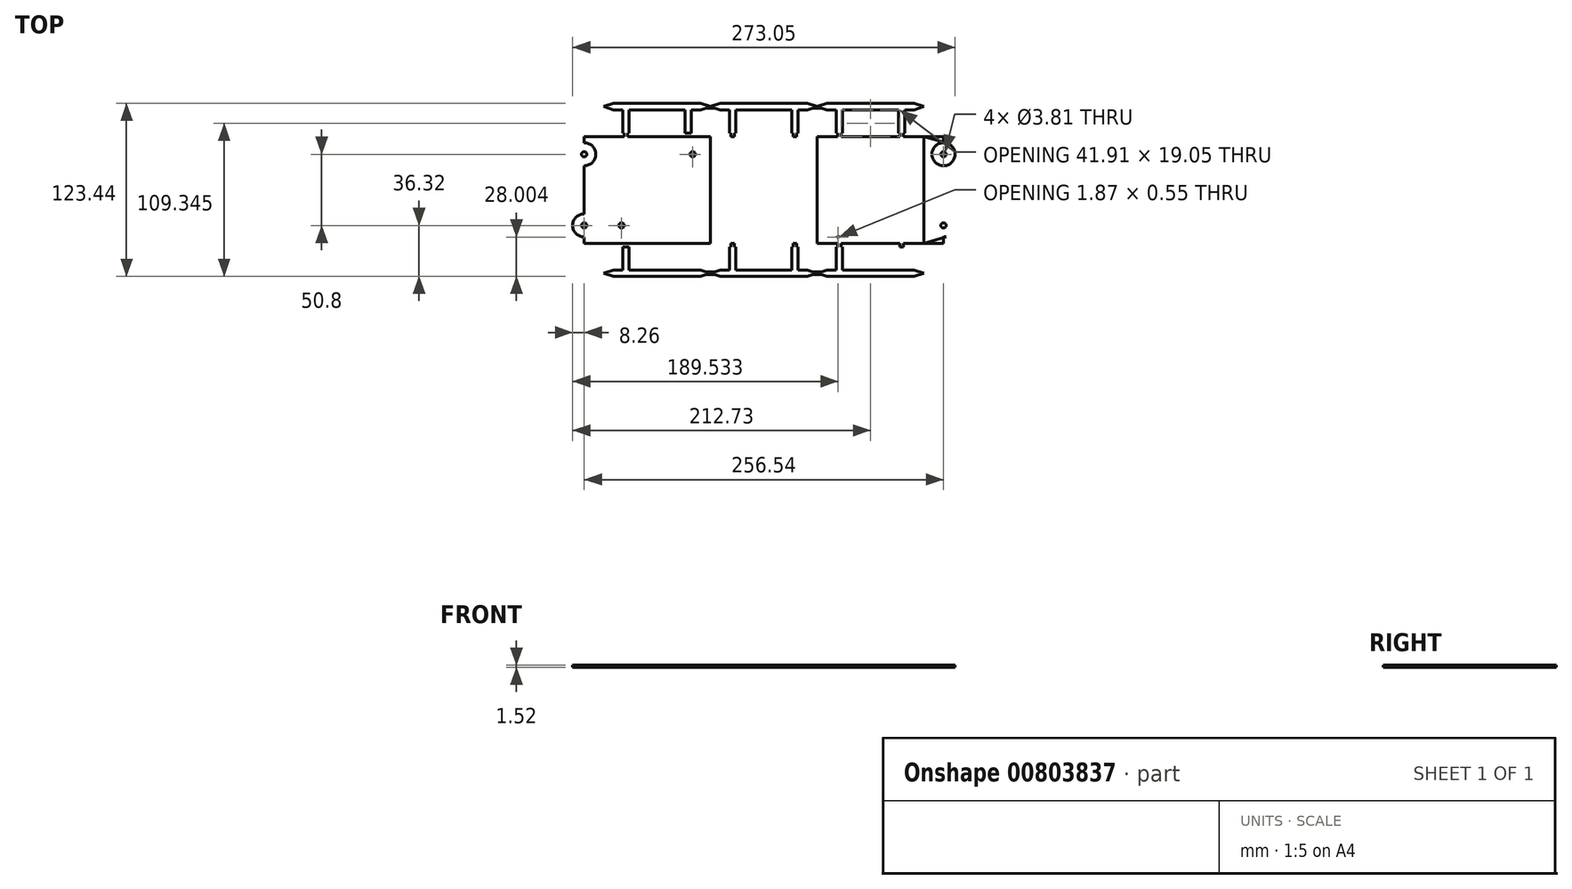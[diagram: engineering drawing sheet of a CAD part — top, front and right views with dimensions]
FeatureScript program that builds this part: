
annotation { "Feature Type Name" : "Feature", "Feature Type Description" : "" }
export const myFeature = defineFeature(function(context is Context, id is Id, definition is map)
    precondition{}
    {
        {
            var Q0;
            Q0=qCreatedBy(makeId("Top.planeOp"),FACE);
            var sketch = newSketch(context, id + "F0", { "sketchPlane" : qUnion([Q0])});
            skLineSegment(sketch, "E0.bottom", {"start": v(38.1, 38.1) * mm, "end": v(-38.1, 38.1) * mm});
            skLineSegment(sketch, "E0.top", {"start": v(38.1, -38.1) * mm, "end": v(-38.1, -38.1) * mm});
            skLineSegment(sketch, "E0.left", {"start": v(38.1, 38.1) * mm, "end": v(38.1, -38.1) * mm});
            skPoint(sketch, "E0.middle", {"position": v(0, 0) * mm});
            skLineSegment(sketch, "E1.bottom", {"start": v(31.75, 31.75) * mm, "end": v(-31.75, 31.75) * mm, "construction": true});
            skLineSegment(sketch, "E1.top", {"start": v(31.75, -31.75) * mm, "end": v(-31.75, -31.75) * mm, "construction": true});
            skLineSegment(sketch, "E1.left", {"start": v(31.75, 31.75) * mm, "end": v(31.75, -31.75) * mm, "construction": true});
            skLineSegment(sketch, "E1.right", {"start": v(-31.75, 31.75) * mm, "end": v(-31.75, -31.75) * mm, "construction": true});
            skLineSegment(sketch, "E2.bottom", {"start": v(-19.18, -31.75) * mm, "end": v(-12.57, -31.75) * mm});
            skLineSegment(sketch, "E2.top", {"start": v(-19.18, -30.23) * mm, "end": v(-12.57, -30.23) * mm});
            skLineSegment(sketch, "E2.left", {"start": v(-19.18, -31.75) * mm, "end": v(-19.18, -30.23) * mm});
            skLineSegment(sketch, "E2.right", {"start": v(-12.57, -31.75) * mm, "end": v(-12.57, -30.23) * mm});
            skPoint(sketch, "E3", {"position": v(-15.88, -31.75) * mm});
            skLineSegment(sketch, "E4.0", {"start": v(-19.43, -29.97) * mm, "end": v(-12.32, -29.97) * mm});
            skLineSegment(sketch, "E4.1", {"start": v(-19.43, -32) * mm, "end": v(-19.43, -29.97) * mm});
            skLineSegment(sketch, "E4.2", {"start": v(-19.43, -32) * mm, "end": v(-12.32, -32) * mm});
            skLineSegment(sketch, "E4.3", {"start": v(-12.32, -32) * mm, "end": v(-12.32, -29.97) * mm});
            skLineSegment(sketch, "E5.MirrorCS", {"start": v(19.43, -29.97) * mm, "end": v(12.32, -29.97) * mm});
            skLineSegment(sketch, "E6.MirrorCS", {"start": v(19.43, -32) * mm, "end": v(19.43, -29.97) * mm});
            skLineSegment(sketch, "E7.MirrorCS", {"start": v(19.43, -32) * mm, "end": v(12.32, -32) * mm});
            skLineSegment(sketch, "E8.MirrorCS", {"start": v(12.32, -32) * mm, "end": v(12.32, -29.97) * mm});
            skLineSegment(sketch, "E9.MirrorCS", {"start": v(-19.43, 32) * mm, "end": v(-19.43, 29.97) * mm});
            skLineSegment(sketch, "E10.MirrorCS", {"start": v(-19.43, 29.97) * mm, "end": v(-12.32, 29.97) * mm});
            skLineSegment(sketch, "E11.MirrorCS", {"start": v(-12.32, 32) * mm, "end": v(-12.32, 29.97) * mm});
            skLineSegment(sketch, "E12.MirrorCS", {"start": v(-19.43, 32) * mm, "end": v(-12.32, 32) * mm});
            skLineSegment(sketch, "E13.MirrorCS", {"start": v(19.43, 29.97) * mm, "end": v(12.32, 29.97) * mm});
            skLineSegment(sketch, "E14.MirrorCS", {"start": v(19.43, 32) * mm, "end": v(19.43, 29.97) * mm});
            skLineSegment(sketch, "E15.MirrorCS", {"start": v(19.43, 32) * mm, "end": v(12.32, 32) * mm});
            skLineSegment(sketch, "E16.MirrorCS", {"start": v(12.32, 32) * mm, "end": v(12.32, 29.97) * mm});
            skLineSegment(sketch, "E17.bottom", {"start": v(-31.75, -19.18) * mm, "end": v(-30.23, -19.18) * mm});
            skLineSegment(sketch, "E17.top", {"start": v(-31.75, -12.57) * mm, "end": v(-30.23, -12.57) * mm});
            skLineSegment(sketch, "E17.left", {"start": v(-31.75, -19.18) * mm, "end": v(-31.75, -12.57) * mm});
            skLineSegment(sketch, "E17.right", {"start": v(-30.23, -19.18) * mm, "end": v(-30.23, -12.57) * mm});
            skPoint(sketch, "E18", {"position": v(-31.75, -15.88) * mm});
            skLineSegment(sketch, "E19.0", {"start": v(-29.97, -19.43) * mm, "end": v(-29.97, -12.32) * mm});
            skLineSegment(sketch, "E19.1", {"start": v(-32, -19.43) * mm, "end": v(-29.97, -19.43) * mm});
            skLineSegment(sketch, "E19.2", {"start": v(-32, -19.43) * mm, "end": v(-32, -12.32) * mm});
            skLineSegment(sketch, "E19.3", {"start": v(-32, -12.32) * mm, "end": v(-29.97, -12.32) * mm});
            skLineSegment(sketch, "E20.MirrorCS", {"start": v(-32, 19.43) * mm, "end": v(-32, 12.32) * mm});
            skLineSegment(sketch, "E21.MirrorCS", {"start": v(-32, 12.32) * mm, "end": v(-29.97, 12.32) * mm});
            skLineSegment(sketch, "E22.MirrorCS", {"start": v(-29.97, 19.43) * mm, "end": v(-29.97, 12.32) * mm});
            skLineSegment(sketch, "E23.MirrorCS", {"start": v(-32, 19.43) * mm, "end": v(-29.97, 19.43) * mm});
            skLineSegment(sketch, "E24.MirrorCS", {"start": v(32, -19.43) * mm, "end": v(32, -12.32) * mm});
            skLineSegment(sketch, "E25.MirrorCS", {"start": v(32, -12.32) * mm, "end": v(29.97, -12.32) * mm});
            skLineSegment(sketch, "E26.MirrorCS", {"start": v(29.97, -19.43) * mm, "end": v(29.97, -12.32) * mm});
            skLineSegment(sketch, "E27.MirrorCS", {"start": v(32, -19.43) * mm, "end": v(29.97, -19.43) * mm});
            skLineSegment(sketch, "E28.MirrorCS", {"start": v(29.97, 19.43) * mm, "end": v(29.97, 12.32) * mm});
            skLineSegment(sketch, "E29.MirrorCS", {"start": v(32, 12.32) * mm, "end": v(29.97, 12.32) * mm});
            skLineSegment(sketch, "E30.MirrorCS", {"start": v(32, 19.43) * mm, "end": v(32, 12.32) * mm});
            skLineSegment(sketch, "E31.MirrorCS", {"start": v(32, 19.43) * mm, "end": v(29.97, 19.43) * mm});
            skLineSegment(sketch, "E32.bottom", {"start": v(-23.5, -38.1) * mm, "end": v(-20.96, -38.1) * mm});
            skLineSegment(sketch, "E32.top", {"start": v(-23.5, -40.64) * mm, "end": v(-20.96, -40.64) * mm});
            skLineSegment(sketch, "E32.left", {"start": v(-23.5, -38.1) * mm, "end": v(-23.5, -40.64) * mm});
            skLineSegment(sketch, "E32.right", {"start": v(-20.96, -38.1) * mm, "end": v(-20.96, -40.64) * mm});
            skPoint(sketch, "E33", {"position": v(-22.23, -38.1) * mm});
            skLineSegment(sketch, "E34.bottom", {"start": v(-24.51, -40.64) * mm, "end": v(-19.94, -40.64) * mm});
            skLineSegment(sketch, "E34.top", {"start": v(-24.51, -57.15) * mm, "end": v(-19.94, -57.15) * mm});
            skLineSegment(sketch, "E34.left", {"start": v(-24.51, -40.64) * mm, "end": v(-24.51, -57.15) * mm});
            skLineSegment(sketch, "E34.right", {"start": v(-19.94, -40.64) * mm, "end": v(-19.94, -57.15) * mm});
            skPoint(sketch, "E35", {"position": v(-22.23, -40.64) * mm});
            skLineSegment(sketch, "E36.MirrorCS", {"start": v(23.5, -38.1) * mm, "end": v(20.96, -38.1) * mm});
            skPoint(sketch, "E37.MirrorP", {"position": v(22.23, -38.1) * mm});
            skLineSegment(sketch, "E38.bottom", {"start": v(0, -57.15) * mm, "end": v(-31.12, -57.15) * mm});
            skLineSegment(sketch, "E38.top", {"start": v(0, -61.72) * mm, "end": v(-31.12, -61.72) * mm});
            skLineSegment(sketch, "E39", {"start": v(-38.1, -59.44) * mm, "end": v(-31.12, -57.15) * mm});
            skLineSegment(sketch, "E40", {"start": v(-38.1, -59.44) * mm, "end": v(-31.12, -61.72) * mm});
            skPoint(sketch, "E41.start.orphan", {"position": v(-31.12, -59.44) * mm});
            skLineSegment(sketch, "E42.MirrorCS", {"start": v(38.1, -38.1) * mm, "end": v(38.1, 38.1) * mm});
            skPoint(sketch, "E43.MirrorP", {"position": v(-38.1, 57.15) * mm});
            skCircle(sketch, "E44", {"center": v(-25.4, 25.4) * mm, "radius": 1.9 * mm});
            skCircle(sketch, "E45.MirrorC", {"center": v(25.4, 25.4) * mm, "radius": 1.9 * mm});
            skCircle(sketch, "E46.MirrorC", {"center": v(-25.4, -25.4) * mm, "radius": 1.9 * mm});
            skCircle(sketch, "E47.MirrorC", {"center": v(25.4, -25.4) * mm, "radius": 1.9 * mm});
            skLineSegment(sketch, "E48", {"start": v(0, 38.1) * mm, "end": v(0, -38.1) * mm, "construction": true});
            skLineSegment(sketch, "E49", {"start": v(0, -38.1) * mm, "end": v(0, -79.98) * mm, "construction": true});
            skLineSegment(sketch, "E50.MirrorCS", {"start": v(24.51, -40.64) * mm, "end": v(19.94, -40.64) * mm});
            skLineSegment(sketch, "E51.MirrorCS", {"start": v(23.5, -40.64) * mm, "end": v(20.96, -40.64) * mm});
            skLineSegment(sketch, "E52.MirrorCS", {"start": v(23.5, -38.1) * mm, "end": v(23.5, -40.64) * mm});
            skLineSegment(sketch, "E53.MirrorCS", {"start": v(20.96, -38.1) * mm, "end": v(20.96, -40.64) * mm});
            skLineSegment(sketch, "E54.MirrorCS", {"start": v(24.51, -57.15) * mm, "end": v(19.94, -57.15) * mm});
            skPoint(sketch, "E55.MirrorP", {"position": v(22.23, -40.64) * mm});
            skLineSegment(sketch, "E56.MirrorCS", {"start": v(0, -57.15) * mm, "end": v(31.12, -57.15) * mm});
            skLineSegment(sketch, "E57.MirrorCS", {"start": v(38.1, -59.44) * mm, "end": v(31.12, -57.15) * mm});
            skLineSegment(sketch, "E58.MirrorCS", {"start": v(38.1, -59.44) * mm, "end": v(31.12, -61.72) * mm});
            skLineSegment(sketch, "E59.MirrorCS", {"start": v(24.51, -40.64) * mm, "end": v(24.51, -57.15) * mm});
            skLineSegment(sketch, "E60.MirrorCS", {"start": v(0, -61.72) * mm, "end": v(31.12, -61.72) * mm});
            skPoint(sketch, "E61.MirrorP", {"position": v(31.12, -59.44) * mm});
            skLineSegment(sketch, "E62.MirrorCS", {"start": v(19.94, -40.64) * mm, "end": v(19.94, -57.15) * mm});
            skLineSegment(sketch, "E63.MirrorCS", {"start": v(-23.5, 40.64) * mm, "end": v(-20.96, 40.64) * mm});
            skLineSegment(sketch, "E64.MirrorCS", {"start": v(-24.51, 40.64) * mm, "end": v(-19.94, 40.64) * mm});
            skPoint(sketch, "E65.MirrorP", {"position": v(22.23, 38.1) * mm});
            skLineSegment(sketch, "E66.MirrorCS", {"start": v(24.51, 40.64) * mm, "end": v(19.94, 40.64) * mm});
            skLineSegment(sketch, "E67.MirrorCS", {"start": v(23.5, 40.64) * mm, "end": v(20.96, 40.64) * mm});
            skPoint(sketch, "E68.MirrorP", {"position": v(-22.23, 38.1) * mm});
            skPoint(sketch, "E69.MirrorP", {"position": v(22.23, 40.64) * mm});
            skPoint(sketch, "E70.MirrorP", {"position": v(-22.23, 40.64) * mm});
            skLineSegment(sketch, "E71.MirrorCS", {"start": v(24.51, 57.15) * mm, "end": v(19.94, 57.15) * mm});
            skLineSegment(sketch, "E72.MirrorCS", {"start": v(-24.51, 57.15) * mm, "end": v(-19.94, 57.15) * mm});
            skLineSegment(sketch, "E73.MirrorCS", {"start": v(24.51, 40.64) * mm, "end": v(24.51, 57.15) * mm});
            skLineSegment(sketch, "E74.MirrorCS", {"start": v(-24.51, 40.64) * mm, "end": v(-24.51, 57.15) * mm});
            skLineSegment(sketch, "E75.MirrorCS", {"start": v(-19.94, 40.64) * mm, "end": v(-19.94, 57.15) * mm});
            skLineSegment(sketch, "E76.MirrorCS", {"start": v(0, 61.72) * mm, "end": v(31.12, 61.72) * mm});
            skLineSegment(sketch, "E77.MirrorCS", {"start": v(-38.1, 59.44) * mm, "end": v(-31.12, 61.72) * mm});
            skLineSegment(sketch, "E78.MirrorCS", {"start": v(19.94, 40.64) * mm, "end": v(19.94, 57.15) * mm});
            skPoint(sketch, "E79.MirrorP", {"position": v(-31.12, 59.44) * mm});
            skLineSegment(sketch, "E80.MirrorCS", {"start": v(-38.1, 59.44) * mm, "end": v(-31.12, 57.15) * mm});
            skLineSegment(sketch, "E81.MirrorCS", {"start": v(0, 57.15) * mm, "end": v(31.12, 57.15) * mm});
            skLineSegment(sketch, "E82.MirrorCS", {"start": v(38.1, 59.44) * mm, "end": v(31.12, 61.72) * mm});
            skLineSegment(sketch, "E83.MirrorCS", {"start": v(0, 61.72) * mm, "end": v(-31.12, 61.72) * mm});
            skPoint(sketch, "E84.MirrorP", {"position": v(31.12, 59.44) * mm});
            skLineSegment(sketch, "E85.MirrorCS", {"start": v(0, 57.15) * mm, "end": v(-31.12, 57.15) * mm});
            skLineSegment(sketch, "E86.MirrorCS", {"start": v(38.1, 59.44) * mm, "end": v(31.12, 57.15) * mm});
            skLineSegment(sketch, "E87.MirrorCS", {"start": v(-23.5, 38.1) * mm, "end": v(-20.96, 38.1) * mm});
            skLineSegment(sketch, "E88.MirrorCS", {"start": v(-20.96, 38.1) * mm, "end": v(-20.96, 40.64) * mm});
            skLineSegment(sketch, "E89.MirrorCS", {"start": v(-23.5, 38.1) * mm, "end": v(-23.5, 40.64) * mm});
            skLineSegment(sketch, "E90.MirrorCS", {"start": v(23.5, 38.1) * mm, "end": v(20.96, 38.1) * mm});
            skLineSegment(sketch, "E91.MirrorCS", {"start": v(20.96, 38.1) * mm, "end": v(20.96, 40.64) * mm});
            skLineSegment(sketch, "E92.MirrorCS", {"start": v(23.5, 38.1) * mm, "end": v(23.5, 40.64) * mm});
            skLineSegment(sketch, "E93", {"start": v(-38.1, -59.44) * mm, "end": v(38.1, -59.44) * mm});
            skLineSegment(sketch, "E94.0", {"start": v(-38.1, -60.45) * mm, "end": v(38.1, -60.45) * mm});
            skLineSegment(sketch, "E95.0", {"start": v(-38.1, -58.42) * mm, "end": v(38.1, -58.42) * mm});
            skLineSegment(sketch, "E96.MirrorCS", {"start": v(-38.1, 58.42) * mm, "end": v(38.1, 58.42) * mm});
            skLineSegment(sketch, "E97.MirrorCS", {"start": v(-38.1, 60.45) * mm, "end": v(38.1, 60.45) * mm});
            skLineSegment(sketch, "E98.MirrorCS", {"start": v(52.7, 38.1) * mm, "end": v(55.25, 38.1) * mm});
            skLineSegment(sketch, "E99.MirrorCS", {"start": v(52.7, 40.64) * mm, "end": v(55.25, 40.64) * mm});
            skLineSegment(sketch, "E100.MirrorCS", {"start": v(52.7, 38.1) * mm, "end": v(52.7, 40.64) * mm});
            skLineSegment(sketch, "E101.MirrorCS", {"start": v(55.25, 38.1) * mm, "end": v(55.25, 40.64) * mm});
            skLineSegment(sketch, "E102.MirrorCS", {"start": v(99.7, 40.64) * mm, "end": v(97.16, 40.64) * mm});
            skLineSegment(sketch, "E103.MirrorCS", {"start": v(99.7, 38.1) * mm, "end": v(97.16, 38.1) * mm});
            skLineSegment(sketch, "E104.MirrorCS", {"start": v(97.16, 38.1) * mm, "end": v(97.16, 40.64) * mm});
            skLineSegment(sketch, "E105.MirrorCS", {"start": v(100.71, 40.64) * mm, "end": v(96.14, 40.64) * mm});
            skLineSegment(sketch, "E106.MirrorCS", {"start": v(99.7, 38.1) * mm, "end": v(99.7, 40.64) * mm});
            skLineSegment(sketch, "E107.MirrorCS", {"start": v(51.69, 40.64) * mm, "end": v(56.26, 40.64) * mm});
            skPoint(sketch, "E108.MirrorP", {"position": v(98.43, 38.1) * mm});
            skPoint(sketch, "E109.MirrorP", {"position": v(53.98, 40.64) * mm});
            skPoint(sketch, "E110.MirrorP", {"position": v(98.43, 40.64) * mm});
            skPoint(sketch, "E111.MirrorP", {"position": v(53.98, 38.1) * mm});
            skLineSegment(sketch, "E112.MirrorCS", {"start": v(38.1, 59.44) * mm, "end": v(45.08, 57.15) * mm});
            skLineSegment(sketch, "E113.MirrorCS", {"start": v(51.69, 57.15) * mm, "end": v(56.26, 57.15) * mm});
            skLineSegment(sketch, "E114.MirrorCS", {"start": v(100.71, 57.15) * mm, "end": v(96.14, 57.15) * mm});
            skLineSegment(sketch, "E115.MirrorCS", {"start": v(38.1, 59.44) * mm, "end": v(45.08, 61.72) * mm});
            skLineSegment(sketch, "E116.MirrorCS", {"start": v(114.3, 59.44) * mm, "end": v(107.32, 61.72) * mm});
            skLineSegment(sketch, "E117.MirrorCS", {"start": v(114.3, 59.44) * mm, "end": v(107.32, 57.15) * mm});
            skLineSegment(sketch, "E118.MirrorCS", {"start": v(38.1, 38.1) * mm, "end": v(114.3, 38.1) * mm});
            skLineSegment(sketch, "E119.MirrorCS", {"start": v(114.3, 60.45) * mm, "end": v(38.1, 60.45) * mm});
            skPoint(sketch, "E120.MirrorP", {"position": v(114.3, 57.15) * mm});
            skLineSegment(sketch, "E121.MirrorCS", {"start": v(76.2, 57.15) * mm, "end": v(45.08, 57.15) * mm});
            skPoint(sketch, "E122.MirrorP", {"position": v(107.32, 59.44) * mm});
            skPoint(sketch, "E123.MirrorP", {"position": v(45.08, 59.44) * mm});
            skLineSegment(sketch, "E124.MirrorCS", {"start": v(51.69, 40.64) * mm, "end": v(51.69, 57.15) * mm});
            skLineSegment(sketch, "E125.MirrorCS", {"start": v(100.71, 40.64) * mm, "end": v(100.71, 57.15) * mm});
            skLineSegment(sketch, "E126.MirrorCS", {"start": v(56.26, 40.64) * mm, "end": v(56.26, 57.15) * mm});
            skLineSegment(sketch, "E127.MirrorCS", {"start": v(96.14, 40.64) * mm, "end": v(96.14, 57.15) * mm});
            skLineSegment(sketch, "E128.MirrorCS", {"start": v(76.2, 61.72) * mm, "end": v(45.08, 61.72) * mm});
            skLineSegment(sketch, "E129.MirrorCS", {"start": v(76.2, 61.72) * mm, "end": v(107.32, 61.72) * mm});
            skLineSegment(sketch, "E130.MirrorCS", {"start": v(114.3, 58.42) * mm, "end": v(38.1, 58.42) * mm});
            skLineSegment(sketch, "E131.MirrorCS", {"start": v(76.2, 57.15) * mm, "end": v(107.32, 57.15) * mm});
            skLineSegment(sketch, "E132.MirrorCS", {"start": v(52.7, -38.1) * mm, "end": v(55.25, -38.1) * mm});
            skLineSegment(sketch, "E133.MirrorCS", {"start": v(52.7, -40.64) * mm, "end": v(55.25, -40.64) * mm});
            skLineSegment(sketch, "E134.MirrorCS", {"start": v(99.7, -38.1) * mm, "end": v(97.16, -38.1) * mm});
            skLineSegment(sketch, "E135.MirrorCS", {"start": v(55.25, -38.1) * mm, "end": v(55.25, -40.64) * mm});
            skLineSegment(sketch, "E136.MirrorCS", {"start": v(97.16, -38.1) * mm, "end": v(97.16, -40.64) * mm});
            skLineSegment(sketch, "E137.MirrorCS", {"start": v(52.7, -38.1) * mm, "end": v(52.7, -40.64) * mm});
            skLineSegment(sketch, "E138.MirrorCS", {"start": v(99.7, -40.64) * mm, "end": v(97.16, -40.64) * mm});
            skLineSegment(sketch, "E139.MirrorCS", {"start": v(99.7, -38.1) * mm, "end": v(99.7, -40.64) * mm});
            skLineSegment(sketch, "E140.MirrorCS", {"start": v(100.71, -40.64) * mm, "end": v(96.14, -40.64) * mm});
            skLineSegment(sketch, "E141.MirrorCS", {"start": v(51.69, -40.64) * mm, "end": v(56.26, -40.64) * mm});
            skLineSegment(sketch, "E142.MirrorCS", {"start": v(38.1, -59.44) * mm, "end": v(45.08, -61.72) * mm});
            skLineSegment(sketch, "E143.MirrorCS", {"start": v(114.3, -59.44) * mm, "end": v(107.32, -61.72) * mm});
            skLineSegment(sketch, "E144.MirrorCS", {"start": v(38.1, -59.44) * mm, "end": v(45.08, -57.15) * mm});
            skLineSegment(sketch, "E145.MirrorCS", {"start": v(51.69, -57.15) * mm, "end": v(56.26, -57.15) * mm});
            skLineSegment(sketch, "E146.MirrorCS", {"start": v(114.3, -59.44) * mm, "end": v(107.32, -57.15) * mm});
            skLineSegment(sketch, "E147.MirrorCS", {"start": v(100.71, -57.15) * mm, "end": v(96.14, -57.15) * mm});
            skPoint(sketch, "E148.MirrorP", {"position": v(98.42, -40.64) * mm});
            skPoint(sketch, "E149.MirrorP", {"position": v(53.97, -38.1) * mm});
            skPoint(sketch, "E150.MirrorP", {"position": v(53.97, -40.64) * mm});
            skLineSegment(sketch, "E151.MirrorCS", {"start": v(114.3, -59.44) * mm, "end": v(38.1, -59.44) * mm});
            skLineSegment(sketch, "E152.MirrorCS", {"start": v(100.71, -40.64) * mm, "end": v(100.71, -57.15) * mm});
            skLineSegment(sketch, "E153.MirrorCS", {"start": v(38.1, -38.1) * mm, "end": v(114.3, -38.1) * mm});
            skLineSegment(sketch, "E154.MirrorCS", {"start": v(96.14, -40.64) * mm, "end": v(96.14, -57.15) * mm});
            skLineSegment(sketch, "E155.MirrorCS", {"start": v(51.69, -40.64) * mm, "end": v(51.69, -57.15) * mm});
            skPoint(sketch, "E156.MirrorP", {"position": v(98.42, -38.1) * mm});
            skPoint(sketch, "E157.MirrorP", {"position": v(107.32, -59.44) * mm});
            skLineSegment(sketch, "E158.MirrorCS", {"start": v(76.2, -38.1) * mm, "end": v(76.2, -79.98) * mm, "construction": true});
            skPoint(sketch, "E159.MirrorP", {"position": v(92.08, -31.75) * mm});
            skLineSegment(sketch, "E160.MirrorCS", {"start": v(76.2, -61.72) * mm, "end": v(45.08, -61.72) * mm});
            skLineSegment(sketch, "E161.MirrorCS", {"start": v(76.2, -61.72) * mm, "end": v(107.32, -61.72) * mm});
            skLineSegment(sketch, "E162.MirrorCS", {"start": v(76.2, -57.15) * mm, "end": v(107.32, -57.15) * mm});
            skPoint(sketch, "E163.MirrorP", {"position": v(45.08, -59.44) * mm});
            skLineSegment(sketch, "E164.MirrorCS", {"start": v(56.26, -40.64) * mm, "end": v(56.26, -57.15) * mm});
            skLineSegment(sketch, "E165.MirrorCS", {"start": v(76.2, -57.15) * mm, "end": v(45.08, -57.15) * mm});
            skLineSegment(sketch, "E166.MirrorCS", {"start": v(114.3, -60.45) * mm, "end": v(38.1, -60.45) * mm});
            skLineSegment(sketch, "E167.MirrorCS", {"start": v(114.3, -58.42) * mm, "end": v(38.1, -58.42) * mm});
            skLineSegment(sketch, "E168", {"start": v(-38.1, 38.1) * mm, "end": v(-38.1, -38.1) * mm});
            skCircle(sketch, "E169", {"center": v(-52.07, -25.4) * mm, "radius": 1.9 * mm});
            skCircle(sketch, "E170.0", {"center": v(-52.07, -25.4) * mm, "radius": 8.25 * mm});
            skLineSegment(sketch, "E171", {"start": v(-38.1, -38.1) * mm, "end": v(-53.94, -33.44) * mm});
            skCircle(sketch, "E172.MirrorC", {"center": v(-52.07, 25.4) * mm, "radius": 1.9 * mm});
            skCircle(sketch, "E173.MirrorC", {"center": v(-52.07, 25.4) * mm, "radius": 8.25 * mm});
            skLineSegment(sketch, "E174.MirrorCS", {"start": v(-38.1, 38.1) * mm, "end": v(-53.94, 33.44) * mm});
            skLineSegment(sketch, "E175", {"start": v(-52.07, -17.14) * mm, "end": v(-52.07, 17.14) * mm});
            skCircle(sketch, "E176.MirrorC", {"center": v(128.27, -25.4) * mm, "radius": 1.9 * mm});
            skCircle(sketch, "E177.MirrorC", {"center": v(128.27, -25.4) * mm, "radius": 8.25 * mm});
            skCircle(sketch, "E178.MirrorC", {"center": v(128.27, 25.4) * mm, "radius": 1.9 * mm});
            skLineSegment(sketch, "E179.MirrorCS", {"start": v(114.3, 38.1) * mm, "end": v(130.14, 33.44) * mm});
            skCircle(sketch, "E180.MirrorC", {"center": v(128.27, 25.4) * mm, "radius": 8.25 * mm});
            skLineSegment(sketch, "E181.MirrorCS", {"start": v(114.3, 38.1) * mm, "end": v(114.3, -38.1) * mm});
            skLineSegment(sketch, "E182.MirrorCS", {"start": v(114.3, -38.1) * mm, "end": v(130.14, -33.44) * mm});
            skLineSegment(sketch, "E183.MirrorCS", {"start": v(128.27, -17.15) * mm, "end": v(128.27, 17.14) * mm});
            skLineSegment(sketch, "E184", {"start": v(-52.07, -33.65) * mm, "end": v(-52.07, -38.1) * mm});
            skLineSegment(sketch, "E185", {"start": v(-52.07, -38.1) * mm, "end": v(-38.1, -38.1) * mm});
            skLineSegment(sketch, "E186.MirrorCS", {"start": v(-52.07, 38.1) * mm, "end": v(-38.1, 38.1) * mm});
            skLineSegment(sketch, "E187.MirrorCS", {"start": v(-52.07, 33.65) * mm, "end": v(-52.07, 38.1) * mm});
            skLineSegment(sketch, "E188.MirrorCS", {"start": v(128.27, 33.65) * mm, "end": v(128.27, 38.1) * mm});
            skLineSegment(sketch, "E189.MirrorCS", {"start": v(128.27, 38.1) * mm, "end": v(114.3, 38.1) * mm});
            skLineSegment(sketch, "E190.MirrorCS", {"start": v(128.27, -38.1) * mm, "end": v(114.3, -38.1) * mm});
            skLineSegment(sketch, "E191.MirrorCS", {"start": v(128.27, -33.66) * mm, "end": v(128.27, -38.1) * mm});
            skLineSegment(sketch, "E192.MirrorCS", {"start": v(175.9, 40.64) * mm, "end": v(173.36, 40.64) * mm});
            skLineSegment(sketch, "E193.MirrorCS", {"start": v(175.9, 38.1) * mm, "end": v(173.36, 38.1) * mm});
            skLineSegment(sketch, "E194.MirrorCS", {"start": v(176.91, 40.64) * mm, "end": v(172.34, 40.64) * mm});
            skLineSegment(sketch, "E195.MirrorCS", {"start": v(128.9, 38.1) * mm, "end": v(131.45, 38.1) * mm});
            skLineSegment(sketch, "E196.MirrorCS", {"start": v(127.89, 40.64) * mm, "end": v(132.46, 40.64) * mm});
            skLineSegment(sketch, "E197.MirrorCS", {"start": v(128.9, 40.64) * mm, "end": v(131.45, 40.64) * mm});
            skLineSegment(sketch, "E198.MirrorCS", {"start": v(175.9, 38.1) * mm, "end": v(175.9, 40.64) * mm});
            skLineSegment(sketch, "E199.MirrorCS", {"start": v(131.45, 38.1) * mm, "end": v(131.45, 40.64) * mm});
            skLineSegment(sketch, "E200.MirrorCS", {"start": v(128.9, 38.1) * mm, "end": v(128.9, 40.64) * mm});
            skLineSegment(sketch, "E201.MirrorCS", {"start": v(173.36, 38.1) * mm, "end": v(173.36, 40.64) * mm});
            skLineSegment(sketch, "E202.MirrorCS", {"start": v(128.9, -40.64) * mm, "end": v(131.44, -40.64) * mm});
            skLineSegment(sketch, "E203.MirrorCS", {"start": v(175.9, -38.1) * mm, "end": v(173.36, -38.1) * mm});
            skLineSegment(sketch, "E204.MirrorCS", {"start": v(127.89, -40.64) * mm, "end": v(132.46, -40.64) * mm});
            skLineSegment(sketch, "E205.MirrorCS", {"start": v(128.9, -38.1) * mm, "end": v(131.44, -38.1) * mm});
            skLineSegment(sketch, "E206.MirrorCS", {"start": v(175.9, -38.1) * mm, "end": v(175.9, -40.64) * mm});
            skLineSegment(sketch, "E207.MirrorCS", {"start": v(131.44, -38.1) * mm, "end": v(131.44, -40.64) * mm});
            skLineSegment(sketch, "E208.MirrorCS", {"start": v(176.91, -40.64) * mm, "end": v(172.34, -40.64) * mm});
            skLineSegment(sketch, "E209.MirrorCS", {"start": v(128.9, -38.1) * mm, "end": v(128.9, -40.64) * mm});
            skLineSegment(sketch, "E210.MirrorCS", {"start": v(175.9, -40.64) * mm, "end": v(173.36, -40.64) * mm});
            skLineSegment(sketch, "E211.MirrorCS", {"start": v(173.36, -38.1) * mm, "end": v(173.36, -40.64) * mm});
            skPoint(sketch, "E212.MirrorP", {"position": v(130.18, 40.64) * mm});
            skPoint(sketch, "E213.MirrorP", {"position": v(174.63, 38.1) * mm});
            skPoint(sketch, "E214.MirrorP", {"position": v(174.63, 40.64) * mm});
            skLineSegment(sketch, "E215.MirrorCS", {"start": v(114.3, 59.44) * mm, "end": v(121.28, 57.15) * mm});
            skLineSegment(sketch, "E216.MirrorCS", {"start": v(114.3, -59.44) * mm, "end": v(121.28, -57.15) * mm});
            skLineSegment(sketch, "E217.MirrorCS", {"start": v(114.3, -59.44) * mm, "end": v(121.28, -61.72) * mm});
            skLineSegment(sketch, "E218.MirrorCS", {"start": v(127.89, -57.15) * mm, "end": v(132.46, -57.15) * mm});
            skLineSegment(sketch, "E219.MirrorCS", {"start": v(114.3, 59.44) * mm, "end": v(121.28, 61.72) * mm});
            skLineSegment(sketch, "E220.MirrorCS", {"start": v(176.91, 57.15) * mm, "end": v(172.34, 57.15) * mm});
            skLineSegment(sketch, "E221.MirrorCS", {"start": v(190.5, 59.44) * mm, "end": v(183.52, 57.15) * mm});
            skLineSegment(sketch, "E222.MirrorCS", {"start": v(190.5, -59.44) * mm, "end": v(183.52, -61.72) * mm});
            skLineSegment(sketch, "E223.MirrorCS", {"start": v(190.5, -59.44) * mm, "end": v(183.52, -57.15) * mm});
            skLineSegment(sketch, "E224.MirrorCS", {"start": v(176.91, -57.15) * mm, "end": v(172.34, -57.15) * mm});
            skLineSegment(sketch, "E225.MirrorCS", {"start": v(127.89, 57.15) * mm, "end": v(132.46, 57.15) * mm});
            skLineSegment(sketch, "E226.MirrorCS", {"start": v(190.5, 59.44) * mm, "end": v(183.52, 61.72) * mm});
            skLineSegment(sketch, "E227.MirrorCS", {"start": v(114.3, -60.45) * mm, "end": v(190.5, -60.45) * mm});
            skLineSegment(sketch, "E228.MirrorCS", {"start": v(114.3, 58.42) * mm, "end": v(190.5, 58.42) * mm});
            skPoint(sketch, "E229.MirrorP", {"position": v(174.63, -38.1) * mm});
            skPoint(sketch, "E230.MirrorP", {"position": v(130.18, 38.1) * mm});
            skLineSegment(sketch, "E231.MirrorCS", {"start": v(190.5, 38.1) * mm, "end": v(114.3, 38.1) * mm});
            skLineSegment(sketch, "E232.MirrorCS", {"start": v(190.5, -38.1) * mm, "end": v(190.5, 38.1) * mm});
            skPoint(sketch, "E233.MirrorP", {"position": v(130.18, -40.64) * mm});
            skPoint(sketch, "E234.MirrorP", {"position": v(174.63, -40.64) * mm});
            skPoint(sketch, "E235.MirrorP", {"position": v(130.18, -38.1) * mm});
            skLineSegment(sketch, "E236.MirrorCS", {"start": v(152.4, 61.72) * mm, "end": v(121.28, 61.72) * mm});
            skLineSegment(sketch, "E237.MirrorCS", {"start": v(127.89, 40.64) * mm, "end": v(127.89, 57.15) * mm});
            skLineSegment(sketch, "E238.MirrorCS", {"start": v(190.5, 38.1) * mm, "end": v(190.5, -38.1) * mm});
            skLineSegment(sketch, "E239.MirrorCS", {"start": v(152.4, -57.15) * mm, "end": v(121.28, -57.15) * mm});
            skLineSegment(sketch, "E240.MirrorCS", {"start": v(152.4, -61.72) * mm, "end": v(183.52, -61.72) * mm});
            skLineSegment(sketch, "E241.MirrorCS", {"start": v(152.4, 57.15) * mm, "end": v(121.28, 57.15) * mm});
            skPoint(sketch, "E242.MirrorP", {"position": v(183.52, 59.44) * mm});
            skLineSegment(sketch, "E243.MirrorCS", {"start": v(127.89, -40.64) * mm, "end": v(127.89, -57.15) * mm});
            skLineSegment(sketch, "E244.MirrorCS", {"start": v(152.4, -57.15) * mm, "end": v(183.52, -57.15) * mm});
            skPoint(sketch, "E245.MirrorP", {"position": v(121.28, -59.44) * mm});
            skLineSegment(sketch, "E246.MirrorCS", {"start": v(152.4, 57.15) * mm, "end": v(183.52, 57.15) * mm});
            skLineSegment(sketch, "E247.MirrorCS", {"start": v(132.46, 40.64) * mm, "end": v(132.46, 57.15) * mm});
            skLineSegment(sketch, "E248.MirrorCS", {"start": v(152.4, -38.1) * mm, "end": v(152.4, -79.98) * mm, "construction": true});
            skPoint(sketch, "E249.MirrorP", {"position": v(121.28, 59.44) * mm});
            skLineSegment(sketch, "E250.MirrorCS", {"start": v(190.5, -38.1) * mm, "end": v(114.3, -38.1) * mm});
            skLineSegment(sketch, "E251.MirrorCS", {"start": v(114.3, -58.42) * mm, "end": v(190.5, -58.42) * mm});
            skLineSegment(sketch, "E252.MirrorCS", {"start": v(176.91, 40.64) * mm, "end": v(176.91, 57.15) * mm});
            skPoint(sketch, "E253.MirrorP", {"position": v(197.48, -59.44) * mm});
            skLineSegment(sketch, "E254.MirrorCS", {"start": v(176.91, -40.64) * mm, "end": v(176.91, -57.15) * mm});
            skPoint(sketch, "E255.MirrorP", {"position": v(183.52, -59.44) * mm});
            skLineSegment(sketch, "E256.MirrorCS", {"start": v(132.46, -40.64) * mm, "end": v(132.46, -57.15) * mm});
            skLineSegment(sketch, "E257.MirrorCS", {"start": v(172.34, -40.64) * mm, "end": v(172.34, -57.15) * mm});
            skLineSegment(sketch, "E258.MirrorCS", {"start": v(114.3, -59.44) * mm, "end": v(190.5, -59.44) * mm});
            skLineSegment(sketch, "E259.MirrorCS", {"start": v(152.4, -61.72) * mm, "end": v(121.28, -61.72) * mm});
            skPoint(sketch, "E260.MirrorP", {"position": v(136.53, -31.75) * mm});
            skLineSegment(sketch, "E261.MirrorCS", {"start": v(114.3, 60.45) * mm, "end": v(190.5, 60.45) * mm});
            skLineSegment(sketch, "E262.MirrorCS", {"start": v(172.34, 40.64) * mm, "end": v(172.34, 57.15) * mm});
            skPoint(sketch, "E263.MirrorP", {"position": v(197.48, 59.44) * mm});
            skLineSegment(sketch, "E264.MirrorCS", {"start": v(152.4, 61.72) * mm, "end": v(183.52, 61.72) * mm});
            skLineSegment(sketch, "E265", {"start": v(76.2, 38.1) * mm, "end": v(76.2, -38.1) * mm, "construction": true});
            skCircle(sketch, "E266.MirrorC", {"center": v(204.47, -25.4) * mm, "radius": 1.9 * mm});
            skLineSegment(sketch, "E267.MirrorCS", {"start": v(204.47, -33.66) * mm, "end": v(204.47, -38.1) * mm});
            skCircle(sketch, "E268.MirrorC", {"center": v(204.47, 25.4) * mm, "radius": 1.9 * mm});
            skLineSegment(sketch, "E269.MirrorCS", {"start": v(204.47, -38.1) * mm, "end": v(190.5, -38.1) * mm});
            skLineSegment(sketch, "E270.MirrorCS", {"start": v(190.5, -38.1) * mm, "end": v(206.34, -33.44) * mm});
            skLineSegment(sketch, "E271.MirrorCS", {"start": v(204.47, 33.65) * mm, "end": v(204.47, 38.1) * mm});
            skLineSegment(sketch, "E272.MirrorCS", {"start": v(190.5, 38.1) * mm, "end": v(206.34, 33.44) * mm});
            skLineSegment(sketch, "E273.MirrorCS", {"start": v(204.47, -17.15) * mm, "end": v(204.47, 17.14) * mm});
            skLineSegment(sketch, "E274.MirrorCS", {"start": v(204.47, 38.1) * mm, "end": v(190.5, 38.1) * mm});
            skCircle(sketch, "E275.MirrorC", {"center": v(204.47, -25.4) * mm, "radius": 8.25 * mm});
            skCircle(sketch, "E276.MirrorC", {"center": v(204.47, 25.4) * mm, "radius": 8.25 * mm});
            skSolve(sketch);
        }
        {
            var Q0;
            {var subQ1=sQuery(id+"F0.wireOp",EDGE,"E74.MirrorCS");Q0=makeQuery(id+"F0.imprint","IMPRINT",FACE,{"disambiguationData":[TD([[makeQuery(id+"F0.imprint","IMPRINT",EDGE,{"derivedFrom":subQ1}),-1.0]])]});}
            var Q1;
            {var subQ0=sQuery(id+"F0.wireOp",EDGE,"E121.MirrorCS");var subQ3=sQuery(id+"F0.wireOp",EDGE,"E112.MirrorCS");var subQ4=makeQuery(id+"F0.imprint","INTERSECT",VERTEX,{"derivedFrom":[subQ3,subQ0]});Q1=makeQuery(id+"F0.imprint","IMPRINT",FACE,{"disambiguationData":[TD([[makeQuery(id+"F0.imprint","IMPRINT",EDGE,{"disambiguationData":[TD([[subQ4,1.0]])],"derivedFrom":subQ3}),1.0]])]});}
            var Q2;
            {var subQ5=sQuery(id+"F0.wireOp",EDGE,"E85.MirrorCS");var subQ7=sQuery(id+"F0.wireOp",EDGE,"E80.MirrorCS");var subQ8=makeQuery(id+"F0.imprint","INTERSECT",VERTEX,{"derivedFrom":[subQ7,subQ5]});Q2=makeQuery(id+"F0.imprint","IMPRINT",FACE,{"disambiguationData":[TD([[makeQuery(id+"F0.imprint","IMPRINT",EDGE,{"disambiguationData":[TD([[subQ8,1.0]])],"derivedFrom":subQ7}),1.0]])]});}
            var Q3;
            {var subQ6=sQuery(id+"F0.wireOp",EDGE,"E128.MirrorCS");Q3=makeQuery(id+"F0.imprint","IMPRINT",FACE,{"disambiguationData":[TD([[makeQuery(id+"F0.imprint","IMPRINT",EDGE,{"derivedFrom":subQ6}),1.0]])]});}
            var Q4;
            {var subQ1=sQuery(id+"F0.wireOp",EDGE,"E76.MirrorCS");Q4=makeQuery(id+"F0.imprint","IMPRINT",FACE,{"disambiguationData":[TD([[makeQuery(id+"F0.imprint","IMPRINT",EDGE,{"derivedFrom":subQ1}),-1.0]])]});}
            var Q5;
            {var subQ5=sQuery(id+"F0.wireOp",EDGE,"E80.MirrorCS");var subQ6=sQuery(id+"F0.wireOp",EDGE,"E77.MirrorCS");var subQ7=makeQuery(id+"F0.imprint","INTERSECT",VERTEX,{"derivedFrom":[subQ6,subQ5]});Q5=makeQuery(id+"F0.imprint","IMPRINT",FACE,{"disambiguationData":[TD([[makeQuery(id+"F0.imprint","IMPRINT",EDGE,{"disambiguationData":[TD([[subQ7,-1.0]])],"derivedFrom":subQ6}),-1.0]])]});}
            var Q6;
            {var subQ3=sQuery(id+"F0.wireOp",EDGE,"E97.MirrorCS");var subQ5=sQuery(id+"F0.wireOp",EDGE,"E119.MirrorCS");var subQ6=makeQuery(id+"F0.imprint","INTERSECT",VERTEX,{"derivedFrom":[subQ3,subQ5]});Q6=makeQuery(id+"F0.imprint","IMPRINT",FACE,{"disambiguationData":[TD([[makeQuery(id+"F0.imprint","IMPRINT",EDGE,{"disambiguationData":[TD([[subQ6,1.0]])],"derivedFrom":subQ3}),-1.0]])]});}
            var Q7;
            {var subQ5=sQuery(id+"F0.wireOp",EDGE,"E119.MirrorCS");var subQ9=sQuery(id+"F0.wireOp",EDGE,"E115.MirrorCS");var subQ11=makeQuery(id+"F0.imprint","INTERSECT",VERTEX,{"derivedFrom":[subQ9,subQ5]});Q7=makeQuery(id+"F0.imprint","IMPRINT",FACE,{"disambiguationData":[TD([[makeQuery(id+"F0.imprint","IMPRINT",EDGE,{"disambiguationData":[TD([[subQ11,1.0]])],"derivedFrom":subQ5}),1.0]])]});}
            var Q8;
            {var subQ3=sQuery(id+"F0.wireOp",EDGE,"E96.MirrorCS");var subQ5=sQuery(id+"F0.wireOp",EDGE,"E130.MirrorCS");var subQ6=makeQuery(id+"F0.imprint","INTERSECT",VERTEX,{"derivedFrom":[subQ3,subQ5]});Q8=makeQuery(id+"F0.imprint","IMPRINT",FACE,{"disambiguationData":[TD([[makeQuery(id+"F0.imprint","IMPRINT",EDGE,{"disambiguationData":[TD([[subQ6,1.0]])],"derivedFrom":subQ3}),1.0]])]});}
            var Q9;
            {var subQ1=sQuery(id+"F0.wireOp",EDGE,"E73.MirrorCS");Q9=makeQuery(id+"F0.imprint","IMPRINT",FACE,{"disambiguationData":[TD([[makeQuery(id+"F0.imprint","IMPRINT",EDGE,{"derivedFrom":subQ1}),1.0]])]});}
            var Q10;
            {var subQ4=sQuery(id+"F0.wireOp",EDGE,"E124.MirrorCS");Q10=makeQuery(id+"F0.imprint","IMPRINT",FACE,{"disambiguationData":[TD([[makeQuery(id+"F0.imprint","IMPRINT",EDGE,{"derivedFrom":subQ4}),-1.0]])]});}
            var Q11;
            {var subQ4=sQuery(id+"F0.wireOp",EDGE,"E125.MirrorCS");Q11=makeQuery(id+"F0.imprint","IMPRINT",FACE,{"disambiguationData":[TD([[makeQuery(id+"F0.imprint","IMPRINT",EDGE,{"derivedFrom":subQ4}),1.0]])]});}
            var Q12;
            Q12=makeQuery(id+"F0.imprint","IMPRINT",FACE,{"disambiguationData":[TD([[makeQuery(id+"F0.imprint","IMPRINT",EDGE,{"derivedFrom":sQuery(id+"F0.wireOp",EDGE,"E63.MirrorCS")}),-1.0]])]});
            var Q13;
            {var subQ0=sQuery(id+"F0.wireOp",EDGE,"E104.MirrorCS");Q13=makeQuery(id+"F0.imprint","IMPRINT",FACE,{"disambiguationData":[TD([[makeQuery(id+"F0.imprint","IMPRINT",EDGE,{"derivedFrom":subQ0}),-1.0]])]});}
            var Q14;
            Q14=makeQuery(id+"F0.imprint","IMPRINT",FACE,{"disambiguationData":[TD([[makeQuery(id+"F0.imprint","IMPRINT",EDGE,{"derivedFrom":sQuery(id+"F0.wireOp",EDGE,"E90.MirrorCS")}),-1.0]])]});
            var Q15;
            {var subQ0=sQuery(id+"F0.wireOp",EDGE,"E100.MirrorCS");Q15=makeQuery(id+"F0.imprint","IMPRINT",FACE,{"disambiguationData":[TD([[makeQuery(id+"F0.imprint","IMPRINT",EDGE,{"derivedFrom":subQ0}),-1.0]])]});}
            var Q16;
            {var subQ5=sQuery(id+"F0.wireOp",EDGE,"E42.MirrorCS");Q16=makeQuery(id+"F0.imprint","IMPRINT",FACE,{"disambiguationData":[TD([[makeQuery(id+"F0.imprint","IMPRINT",EDGE,{"derivedFrom":subQ5}),-1.0]])]});}
            var Q17;
            {var subQ4=sQuery(id+"F0.wireOp",EDGE,"E152.MirrorCS");Q17=makeQuery(id+"F0.imprint","IMPRINT",FACE,{"disambiguationData":[TD([[makeQuery(id+"F0.imprint","IMPRINT",EDGE,{"derivedFrom":subQ4}),-1.0]])]});}
            var Q18;
            {var subQ0=sQuery(id+"F0.wireOp",EDGE,"E155.MirrorCS");Q18=makeQuery(id+"F0.imprint","IMPRINT",FACE,{"disambiguationData":[TD([[makeQuery(id+"F0.imprint","IMPRINT",EDGE,{"derivedFrom":subQ0}),1.0]])]});}
            var Q19;
            {var subQ0=sQuery(id+"F0.wireOp",EDGE,"E151.MirrorCS");Q19=makeQuery(id+"F0.imprint","IMPRINT",FACE,{"disambiguationData":[TD([[makeQuery(id+"F0.imprint","IMPRINT",EDGE,{"derivedFrom":subQ0}),-1.0]])]});}
            var Q20;
            {var subQ0=sQuery(id+"F0.wireOp",EDGE,"E160.MirrorCS");Q20=makeQuery(id+"F0.imprint","IMPRINT",FACE,{"disambiguationData":[TD([[makeQuery(id+"F0.imprint","IMPRINT",EDGE,{"derivedFrom":subQ0}),-1.0]])]});}
            var Q21;
            {var subQ2=sQuery(id+"F0.wireOp",EDGE,"E165.MirrorCS");var subQ5=sQuery(id+"F0.wireOp",EDGE,"E144.MirrorCS");var subQ11=makeQuery(id+"F0.imprint","INTERSECT",VERTEX,{"derivedFrom":[subQ5,subQ2]});Q21=makeQuery(id+"F0.imprint","IMPRINT",FACE,{"disambiguationData":[TD([[makeQuery(id+"F0.imprint","IMPRINT",EDGE,{"disambiguationData":[TD([[subQ11,1.0]])],"derivedFrom":subQ5}),-1.0]])]});}
            var Q22;
            {var subQ0=sQuery(id+"F0.wireOp",EDGE,"E151.MirrorCS");Q22=makeQuery(id+"F0.imprint","IMPRINT",FACE,{"disambiguationData":[TD([[makeQuery(id+"F0.imprint","IMPRINT",EDGE,{"derivedFrom":subQ0}),1.0]])]});}
            var Q23;
            {var subQ0=sQuery(id+"F0.wireOp",EDGE,"E136.MirrorCS");Q23=makeQuery(id+"F0.imprint","IMPRINT",FACE,{"disambiguationData":[TD([[makeQuery(id+"F0.imprint","IMPRINT",EDGE,{"derivedFrom":subQ0}),1.0]])]});}
            var Q24;
            {var subQ0=sQuery(id+"F0.wireOp",EDGE,"E135.MirrorCS");Q24=makeQuery(id+"F0.imprint","IMPRINT",FACE,{"disambiguationData":[TD([[makeQuery(id+"F0.imprint","IMPRINT",EDGE,{"derivedFrom":subQ0}),-1.0]])]});}
            var Q25;
            {var subQ3=sQuery(id+"F0.wireOp",EDGE,"E51.MirrorCS");Q25=makeQuery(id+"F0.imprint","IMPRINT",FACE,{"disambiguationData":[TD([[makeQuery(id+"F0.imprint","IMPRINT",EDGE,{"derivedFrom":subQ3}),1.0]])]});}
            var Q26;
            {var subQ0=sQuery(id+"F0.wireOp",EDGE,"E34.left");Q26=makeQuery(id+"F0.imprint","IMPRINT",FACE,{"disambiguationData":[TD([[makeQuery(id+"F0.imprint","IMPRINT",EDGE,{"derivedFrom":subQ0}),1.0]])]});}
            var Q27;
            {var subQ0=sQuery(id+"F0.wireOp",EDGE,"E93");Q27=makeQuery(id+"F0.imprint","IMPRINT",FACE,{"disambiguationData":[TD([[makeQuery(id+"F0.imprint","IMPRINT",EDGE,{"derivedFrom":subQ0}),1.0]])]});}
            var Q28;
            {var subQ0=sQuery(id+"F0.wireOp",EDGE,"E38.bottom");var subQ8=makeQuery(id+"F0.imprint","INTERSECT",VERTEX,{"derivedFrom":[sQuery(id+"F0.wireOp",EDGE,"E34.right"),subQ0]});Q28=makeQuery(id+"F0.imprint","IMPRINT",FACE,{"disambiguationData":[TD([[makeQuery(id+"F0.imprint","IMPRINT",EDGE,{"disambiguationData":[TD([[subQ8,1.0]])],"derivedFrom":subQ0}),1.0]])]});}
            var Q29;
            {var subQ2=sQuery(id+"F0.wireOp",EDGE,"E38.top");Q29=makeQuery(id+"F0.imprint","IMPRINT",FACE,{"disambiguationData":[TD([[makeQuery(id+"F0.imprint","IMPRINT",EDGE,{"derivedFrom":subQ2}),-1.0]])]});}
            var Q30;
            {var subQ0=sQuery(id+"F0.wireOp",EDGE,"E93");Q30=makeQuery(id+"F0.imprint","IMPRINT",FACE,{"disambiguationData":[TD([[makeQuery(id+"F0.imprint","IMPRINT",EDGE,{"derivedFrom":subQ0}),-1.0]])]});}
            var Q31;
            {var subQ3=sQuery(id+"F0.wireOp",EDGE,"E95.0");var subQ5=sQuery(id+"F0.wireOp",EDGE,"E167.MirrorCS");var subQ6=makeQuery(id+"F0.imprint","INTERSECT",VERTEX,{"derivedFrom":[subQ3,subQ5]});Q31=makeQuery(id+"F0.imprint","IMPRINT",FACE,{"disambiguationData":[TD([[makeQuery(id+"F0.imprint","IMPRINT",EDGE,{"disambiguationData":[TD([[subQ6,1.0]])],"derivedFrom":subQ3}),-1.0]])]});}
            var Q32;
            {var subQ3=sQuery(id+"F0.wireOp",EDGE,"E94.0");var subQ5=sQuery(id+"F0.wireOp",EDGE,"E166.MirrorCS");var subQ6=makeQuery(id+"F0.imprint","INTERSECT",VERTEX,{"derivedFrom":[subQ3,subQ5]});Q32=makeQuery(id+"F0.imprint","IMPRINT",FACE,{"disambiguationData":[TD([[makeQuery(id+"F0.imprint","IMPRINT",EDGE,{"disambiguationData":[TD([[subQ6,1.0]])],"derivedFrom":subQ3}),1.0]])]});}
            var Q33;
            Q33=makeQuery(id+"F0.imprint","IMPRINT",FACE,{"disambiguationData":[TD([[makeQuery(id+"F0.imprint","IMPRINT",EDGE,{"derivedFrom":sQuery(id+"F0.wireOp",EDGE,"E32.bottom")}),-1.0]])]});
            var Q34;
            Q34=makeQuery(id+"F0.imprint","IMPRINT",FACE,{"disambiguationData":[TD([[makeQuery(id+"F0.imprint","IMPRINT",EDGE,{"derivedFrom":sQuery(id+"F0.wireOp",EDGE,"E51.MirrorCS")}),-1.0]])]});
            var Q35;
            Q35=makeQuery(id+"F0.imprint","IMPRINT",FACE,{"disambiguationData":[TD([[makeQuery(id+"F0.imprint","IMPRINT",EDGE,{"derivedFrom":sQuery(id+"F0.wireOp",EDGE,"E13.MirrorCS")}),-1.0]])]});
            var Q36;
            Q36=makeQuery(id+"F0.imprint","IMPRINT",FACE,{"disambiguationData":[TD([[makeQuery(id+"F0.imprint","IMPRINT",EDGE,{"derivedFrom":sQuery(id+"F0.wireOp",EDGE,"E5.MirrorCS")}),1.0]])]});
            var Q37;
            Q37=makeQuery(id+"F0.imprint","IMPRINT",FACE,{"disambiguationData":[TD([[makeQuery(id+"F0.imprint","IMPRINT",EDGE,{"derivedFrom":sQuery(id+"F0.wireOp",EDGE,"E9.MirrorCS")}),1.0]])]});
            var Q38;
            Q38=makeQuery(id+"F0.imprint","IMPRINT",FACE,{"disambiguationData":[TD([[makeQuery(id+"F0.imprint","IMPRINT",EDGE,{"derivedFrom":sQuery(id+"F0.wireOp",EDGE,"E20.MirrorCS")}),1.0]])]});
            var Q39;
            Q39=makeQuery(id+"F0.imprint","IMPRINT",FACE,{"disambiguationData":[TD([[makeQuery(id+"F0.imprint","IMPRINT",EDGE,{"derivedFrom":sQuery(id+"F0.wireOp",EDGE,"E24.MirrorCS")}),1.0]])]});
            var Q40;
            Q40=makeQuery(id+"F0.imprint","IMPRINT",FACE,{"disambiguationData":[TD([[makeQuery(id+"F0.imprint","IMPRINT",EDGE,{"derivedFrom":sQuery(id+"F0.wireOp",EDGE,"E28.MirrorCS")}),1.0]])]});
            var Q41;
            Q41=makeQuery(id+"F0.imprint","IMPRINT",FACE,{"disambiguationData":[TD([[makeQuery(id+"F0.imprint","IMPRINT",EDGE,{"derivedFrom":sQuery(id+"F0.wireOp",EDGE,"E4.0")}),1.0]])]});
            var Q42;
            Q42=makeQuery(id+"F0.imprint","IMPRINT",FACE,{"disambiguationData":[TD([[makeQuery(id+"F0.imprint","IMPRINT",EDGE,{"derivedFrom":sQuery(id+"F0.wireOp",EDGE,"E2.bottom")}),1.0]])]});
            var Q43;
            Q43=makeQuery(id+"F0.imprint","IMPRINT",FACE,{"disambiguationData":[TD([[makeQuery(id+"F0.imprint","IMPRINT",EDGE,{"derivedFrom":sQuery(id+"F0.wireOp",EDGE,"E44")}),1.0]])]});
            var Q44;
            Q44=makeQuery(id+"F0.imprint","IMPRINT",FACE,{"disambiguationData":[TD([[makeQuery(id+"F0.imprint","IMPRINT",EDGE,{"derivedFrom":sQuery(id+"F0.wireOp",EDGE,"E45.MirrorC")}),-1.0]])]});
            var Q45;
            Q45=makeQuery(id+"F0.imprint","IMPRINT",FACE,{"disambiguationData":[TD([[makeQuery(id+"F0.imprint","IMPRINT",EDGE,{"derivedFrom":sQuery(id+"F0.wireOp",EDGE,"E46.MirrorC")}),-1.0]])]});
            var Q46;
            Q46=makeQuery(id+"F0.imprint","IMPRINT",FACE,{"disambiguationData":[TD([[makeQuery(id+"F0.imprint","IMPRINT",EDGE,{"derivedFrom":sQuery(id+"F0.wireOp",EDGE,"E47.MirrorC")}),1.0]])]});
            var Q47;
            Q47=makeQuery(id+"F0.imprint","IMPRINT",FACE,{"disambiguationData":[TD([[makeQuery(id+"F0.imprint","IMPRINT",EDGE,{"derivedFrom":sQuery(id+"F0.wireOp",EDGE,"E17.bottom")}),1.0]])]});
            var Q48;
            Q48=makeQuery(id+"F0.imprint","IMPRINT",FACE,{"disambiguationData":[TD([[makeQuery(id+"F0.imprint","IMPRINT",EDGE,{"derivedFrom":sQuery(id+"F0.wireOp",EDGE,"E17.bottom")}),-1.0]])]});
            var Q49;
            Q49=makeQuery(id+"F0.imprint","IMPRINT",FACE,{"disambiguationData":[TD([[makeQuery(id+"F0.imprint","IMPRINT",EDGE,{"derivedFrom":sQuery(id+"F0.wireOp",EDGE,"E2.bottom")}),-1.0]])]});
            var Q50;
            {var subQ10=sQuery(id+"F0.wireOp",EDGE,"E168");Q50=makeQuery(id+"F0.imprint","IMPRINT",FACE,{"disambiguationData":[TD([[makeQuery(id+"F0.imprint","IMPRINT",EDGE,{"derivedFrom":subQ10}),-1.0]])]});}
            var Q51;
            Q51=makeQuery(id+"F0.imprint","IMPRINT",FACE,{"disambiguationData":[TD([[makeQuery(id+"F0.imprint","IMPRINT",EDGE,{"derivedFrom":sQuery(id+"F0.wireOp",EDGE,"E172.MirrorC")}),1.0]])]});
            var Q52;
            Q52=makeQuery(id+"F0.imprint","IMPRINT",FACE,{"disambiguationData":[TD([[makeQuery(id+"F0.imprint","IMPRINT",EDGE,{"derivedFrom":sQuery(id+"F0.wireOp",EDGE,"E169")}),-1.0]])]});
            var Q53;
            {var subQ0=sQuery(id+"F0.wireOp",EDGE,"E180.MirrorC");var subQ1=sQuery(id+"F0.wireOp",EDGE,"E179.MirrorCS");var subQ2=makeQuery(id+"F0.imprint","INTERSECT",VERTEX,{"derivedFrom":[subQ1,subQ0]});Q53=makeQuery(id+"F0.imprint","IMPRINT",FACE,{"disambiguationData":[TD([[makeQuery(id+"F0.imprint","IMPRINT",EDGE,{"disambiguationData":[TD([[subQ2,1.0]])],"derivedFrom":subQ1}),-1.0]])]});}
            var Q54;
            Q54=makeQuery(id+"F0.imprint","IMPRINT",FACE,{"disambiguationData":[TD([[makeQuery(id+"F0.imprint","IMPRINT",EDGE,{"derivedFrom":sQuery(id+"F0.wireOp",EDGE,"E176.MirrorC")}),1.0]])]});
            var Q55;
            Q55=makeQuery(id+"F0.imprint","IMPRINT",FACE,{"disambiguationData":[TD([[makeQuery(id+"F0.imprint","IMPRINT",EDGE,{"derivedFrom":sQuery(id+"F0.wireOp",EDGE,"E178.MirrorC")}),-1.0]])]});
            var Q56;
            {var subQ6=sQuery(id+"F0.wireOp",EDGE,"E181.MirrorCS");Q56=makeQuery(id+"F0.imprint","IMPRINT",FACE,{"disambiguationData":[TD([[makeQuery(id+"F0.imprint","IMPRINT",EDGE,{"derivedFrom":subQ6}),1.0]])]});}
            var Q57;
            {var subQ0=sQuery(id+"F0.wireOp",EDGE,"E186.MirrorCS");Q57=makeQuery(id+"F0.imprint","IMPRINT",FACE,{"disambiguationData":[TD([[makeQuery(id+"F0.imprint","IMPRINT",EDGE,{"derivedFrom":subQ0}),-1.0]])]});}
            var Q58;
            {var subQ0=sQuery(id+"F0.wireOp",EDGE,"E185");Q58=makeQuery(id+"F0.imprint","IMPRINT",FACE,{"disambiguationData":[TD([[makeQuery(id+"F0.imprint","IMPRINT",EDGE,{"derivedFrom":subQ0}),1.0]])]});}
            var Q59;
            {var subQ0=sQuery(id+"F0.wireOp",EDGE,"E192.MirrorCS");Q59=makeQuery(id+"F0.imprint","IMPRINT",FACE,{"disambiguationData":[TD([[makeQuery(id+"F0.imprint","IMPRINT",EDGE,{"derivedFrom":subQ0}),-1.0]])]});}
            var Q60;
            Q60=makeQuery(id+"F0.imprint","IMPRINT",FACE,{"disambiguationData":[TD([[makeQuery(id+"F0.imprint","IMPRINT",EDGE,{"derivedFrom":sQuery(id+"F0.wireOp",EDGE,"E268.MirrorC")}),-1.0]])]});
            var Q61;
            {var subQ0=sQuery(id+"F0.wireOp",EDGE,"E231.MirrorCS");var subQ3=sQuery(id+"F0.wireOp",EDGE,"E188.MirrorCS");var subQ5=makeQuery(id+"F0.imprint","INTERSECT",VERTEX,{"derivedFrom":[subQ3,subQ0]});Q61=makeQuery(id+"F0.imprint","IMPRINT",FACE,{"disambiguationData":[TD([[makeQuery(id+"F0.imprint","IMPRINT",EDGE,{"disambiguationData":[TD([[subQ5,1.0]])],"derivedFrom":subQ3}),1.0]])]});}
            var Q62;
            {var subQ0=sQuery(id+"F0.wireOp",EDGE,"E243.MirrorCS");Q62=makeQuery(id+"F0.imprint","IMPRINT",FACE,{"disambiguationData":[TD([[makeQuery(id+"F0.imprint","IMPRINT",EDGE,{"derivedFrom":subQ0}),1.0]])]});}
            var Q63;
            {var subQ0=sQuery(id+"F0.wireOp",EDGE,"E250.MirrorCS");var subQ3=sQuery(id+"F0.wireOp",EDGE,"E191.MirrorCS");var subQ5=makeQuery(id+"F0.imprint","INTERSECT",VERTEX,{"derivedFrom":[subQ3,subQ0]});Q63=makeQuery(id+"F0.imprint","IMPRINT",FACE,{"disambiguationData":[TD([[makeQuery(id+"F0.imprint","IMPRINT",EDGE,{"disambiguationData":[TD([[subQ5,1.0]])],"derivedFrom":subQ3}),-1.0]])]});}
            var Q64;
            {var subQ7=sQuery(id+"F0.wireOp",EDGE,"E183.MirrorCS");Q64=makeQuery(id+"F0.imprint","IMPRINT",FACE,{"disambiguationData":[TD([[makeQuery(id+"F0.imprint","IMPRINT",EDGE,{"derivedFrom":subQ7}),-1.0]])]});}
            var Q65;
            {var subQ0=sQuery(id+"F0.wireOp",EDGE,"E269.MirrorCS");Q65=makeQuery(id+"F0.imprint","IMPRINT",FACE,{"disambiguationData":[TD([[makeQuery(id+"F0.imprint","IMPRINT",EDGE,{"derivedFrom":subQ0}),-1.0]])]});}
            var Q66;
            {var subQ3=sQuery(id+"F0.wireOp",EDGE,"E210.MirrorCS");Q66=makeQuery(id+"F0.imprint","IMPRINT",FACE,{"disambiguationData":[TD([[makeQuery(id+"F0.imprint","IMPRINT",EDGE,{"derivedFrom":subQ3}),1.0]])]});}
            var Q67;
            {var subQ3=sQuery(id+"F0.wireOp",EDGE,"E237.MirrorCS");Q67=makeQuery(id+"F0.imprint","IMPRINT",FACE,{"disambiguationData":[TD([[makeQuery(id+"F0.imprint","IMPRINT",EDGE,{"derivedFrom":subQ3}),-1.0]])]});}
            var Q68;
            {var subQ0=sQuery(id+"F0.wireOp",EDGE,"E238.MirrorCS");Q68=makeQuery(id+"F0.imprint","IMPRINT",FACE,{"disambiguationData":[TD([[makeQuery(id+"F0.imprint","IMPRINT",EDGE,{"derivedFrom":subQ0}),1.0]])]});}
            var Q69;
            Q69=makeQuery(id+"F0.imprint","IMPRINT",FACE,{"disambiguationData":[TD([[makeQuery(id+"F0.imprint","IMPRINT",EDGE,{"derivedFrom":sQuery(id+"F0.wireOp",EDGE,"E266.MirrorC")}),1.0]])]});
            var Q70;
            {var subQ0=sQuery(id+"F0.wireOp",EDGE,"E274.MirrorCS");Q70=makeQuery(id+"F0.imprint","IMPRINT",FACE,{"disambiguationData":[TD([[makeQuery(id+"F0.imprint","IMPRINT",EDGE,{"derivedFrom":subQ0}),1.0]])]});}
            var Q71;
            {var subQ1=sQuery(id+"F0.wireOp",EDGE,"E241.MirrorCS");var subQ7=sQuery(id+"F0.wireOp",EDGE,"E215.MirrorCS");var subQ11=makeQuery(id+"F0.imprint","INTERSECT",VERTEX,{"derivedFrom":[subQ7,subQ1]});Q71=makeQuery(id+"F0.imprint","IMPRINT",FACE,{"disambiguationData":[TD([[makeQuery(id+"F0.imprint","IMPRINT",EDGE,{"disambiguationData":[TD([[subQ11,1.0]])],"derivedFrom":subQ7}),1.0]])]});}
            var Q72;
            {var subQ0=sQuery(id+"F0.wireOp",EDGE,"E258.MirrorCS");Q72=makeQuery(id+"F0.imprint","IMPRINT",FACE,{"disambiguationData":[TD([[makeQuery(id+"F0.imprint","IMPRINT",EDGE,{"derivedFrom":subQ0}),1.0]])]});}
            var Q73;
            {var subQ0=sQuery(id+"F0.wireOp",EDGE,"E226.MirrorCS");var subQ1=sQuery(id+"F0.wireOp",EDGE,"E221.MirrorCS");var subQ2=makeQuery(id+"F0.imprint","INTERSECT",VERTEX,{"derivedFrom":[subQ1,subQ0]});Q73=makeQuery(id+"F0.imprint","IMPRINT",FACE,{"disambiguationData":[TD([[makeQuery(id+"F0.imprint","IMPRINT",EDGE,{"disambiguationData":[TD([[subQ2,-1.0]])],"derivedFrom":subQ1}),-1.0]])]});}
            var Q74;
            {var subQ0=sQuery(id+"F0.wireOp",EDGE,"E275.MirrorC");var subQ1=sQuery(id+"F0.wireOp",EDGE,"E267.MirrorCS");var subQ2=makeQuery(id+"F0.imprint","INTERSECT",VERTEX,{"derivedFrom":[subQ1,subQ0]});Q74=makeQuery(id+"F0.imprint","IMPRINT",FACE,{"disambiguationData":[TD([[makeQuery(id+"F0.imprint","IMPRINT",EDGE,{"disambiguationData":[TD([[subQ2,-1.0]])],"derivedFrom":subQ1}),1.0]])]});}
            var Q75;
            {var subQ0=sQuery(id+"F0.wireOp",EDGE,"E276.MirrorC");var subQ1=sQuery(id+"F0.wireOp",EDGE,"E271.MirrorCS");var subQ2=makeQuery(id+"F0.imprint","INTERSECT",VERTEX,{"derivedFrom":[subQ1,subQ0]});Q75=makeQuery(id+"F0.imprint","IMPRINT",FACE,{"disambiguationData":[TD([[makeQuery(id+"F0.imprint","IMPRINT",EDGE,{"disambiguationData":[TD([[subQ2,-1.0]])],"derivedFrom":subQ1}),-1.0]])]});}
            var Q76;
            {var subQ1=sQuery(id+"F0.wireOp",EDGE,"E239.MirrorCS");var subQ9=sQuery(id+"F0.wireOp",EDGE,"E216.MirrorCS");var subQ10=makeQuery(id+"F0.imprint","INTERSECT",VERTEX,{"derivedFrom":[subQ9,subQ1]});Q76=makeQuery(id+"F0.imprint","IMPRINT",FACE,{"disambiguationData":[TD([[makeQuery(id+"F0.imprint","IMPRINT",EDGE,{"disambiguationData":[TD([[subQ10,1.0]])],"derivedFrom":subQ9}),-1.0]])]});}
            var Q77;
            {var subQ5=sQuery(id+"F0.wireOp",EDGE,"E236.MirrorCS");Q77=makeQuery(id+"F0.imprint","IMPRINT",FACE,{"disambiguationData":[TD([[makeQuery(id+"F0.imprint","IMPRINT",EDGE,{"derivedFrom":subQ5}),1.0]])]});}
            var Q78;
            {var subQ0=sQuery(id+"F0.wireOp",EDGE,"E182.MirrorCS");var subQ1=sQuery(id+"F0.wireOp",EDGE,"E177.MirrorC");var subQ2=makeQuery(id+"F0.imprint","INTERSECT",VERTEX,{"derivedFrom":[subQ1,subQ0]});Q78=makeQuery(id+"F0.imprint","IMPRINT",FACE,{"disambiguationData":[TD([[makeQuery(id+"F0.imprint","IMPRINT",EDGE,{"disambiguationData":[TD([[subQ2,-1.0]])],"derivedFrom":subQ1}),1.0]])]});}
            var Q79;
            {var subQ0=sQuery(id+"F0.wireOp",EDGE,"E258.MirrorCS");Q79=makeQuery(id+"F0.imprint","IMPRINT",FACE,{"disambiguationData":[TD([[makeQuery(id+"F0.imprint","IMPRINT",EDGE,{"derivedFrom":subQ0}),-1.0]])]});}
            var Q80;
            {var subQ5=sQuery(id+"F0.wireOp",EDGE,"E240.MirrorCS");Q80=makeQuery(id+"F0.imprint","IMPRINT",FACE,{"disambiguationData":[TD([[makeQuery(id+"F0.imprint","IMPRINT",EDGE,{"derivedFrom":subQ5}),1.0]])]});}
            var Q81;
            {var subQ3=sQuery(id+"F0.wireOp",EDGE,"E167.MirrorCS");var subQ5=sQuery(id+"F0.wireOp",EDGE,"E251.MirrorCS");var subQ6=makeQuery(id+"F0.imprint","INTERSECT",VERTEX,{"derivedFrom":[subQ3,subQ5]});Q81=makeQuery(id+"F0.imprint","IMPRINT",FACE,{"disambiguationData":[TD([[makeQuery(id+"F0.imprint","IMPRINT",EDGE,{"disambiguationData":[TD([[subQ6,-1.0]])],"derivedFrom":subQ3}),1.0]])]});}
            var Q82;
            Q82=makeQuery(id+"F0.imprint","IMPRINT",FACE,{"disambiguationData":[TD([[makeQuery(id+"F0.imprint","IMPRINT",EDGE,{"derivedFrom":sQuery(id+"F0.wireOp",EDGE,"E176.MirrorC")}),-1.0]])]});
            var Q83;
            Q83=makeQuery(id+"F0.imprint","IMPRINT",FACE,{"disambiguationData":[TD([[makeQuery(id+"F0.imprint","IMPRINT",EDGE,{"derivedFrom":sQuery(id+"F0.wireOp",EDGE,"E178.MirrorC")}),1.0]])]});
            var Q84;
            {var subQ3=sQuery(id+"F0.wireOp",EDGE,"E166.MirrorCS");var subQ5=sQuery(id+"F0.wireOp",EDGE,"E227.MirrorCS");var subQ6=makeQuery(id+"F0.imprint","INTERSECT",VERTEX,{"derivedFrom":[subQ3,subQ5]});Q84=makeQuery(id+"F0.imprint","IMPRINT",FACE,{"disambiguationData":[TD([[makeQuery(id+"F0.imprint","IMPRINT",EDGE,{"disambiguationData":[TD([[subQ6,-1.0]])],"derivedFrom":subQ3}),-1.0]])]});}
            var Q85;
            {var subQ3=sQuery(id+"F0.wireOp",EDGE,"E119.MirrorCS");var subQ5=sQuery(id+"F0.wireOp",EDGE,"E261.MirrorCS");var subQ6=makeQuery(id+"F0.imprint","INTERSECT",VERTEX,{"derivedFrom":[subQ3,subQ5]});Q85=makeQuery(id+"F0.imprint","IMPRINT",FACE,{"disambiguationData":[TD([[makeQuery(id+"F0.imprint","IMPRINT",EDGE,{"disambiguationData":[TD([[subQ6,-1.0]])],"derivedFrom":subQ3}),1.0]])]});}
            var Q86;
            {var subQ3=sQuery(id+"F0.wireOp",EDGE,"E130.MirrorCS");var subQ5=sQuery(id+"F0.wireOp",EDGE,"E228.MirrorCS");var subQ7=makeQuery(id+"F0.imprint","INTERSECT",VERTEX,{"derivedFrom":[subQ3,subQ5]});Q86=makeQuery(id+"F0.imprint","IMPRINT",FACE,{"disambiguationData":[TD([[makeQuery(id+"F0.imprint","IMPRINT",EDGE,{"disambiguationData":[TD([[subQ7,-1.0]])],"derivedFrom":subQ3}),-1.0]])]});}
            var Q87;
            {var subQ0=sQuery(id+"F0.wireOp",EDGE,"E206.MirrorCS");Q87=makeQuery(id+"F0.imprint","IMPRINT",FACE,{"disambiguationData":[TD([[makeQuery(id+"F0.imprint","IMPRINT",EDGE,{"derivedFrom":subQ0}),-1.0]])]});}
            var Q88;
            {var subQ0=sQuery(id+"F0.wireOp",EDGE,"E198.MirrorCS");Q88=makeQuery(id+"F0.imprint","IMPRINT",FACE,{"disambiguationData":[TD([[makeQuery(id+"F0.imprint","IMPRINT",EDGE,{"derivedFrom":subQ0}),1.0]])]});}
            var Q89;
            {var subQ0=sQuery(id+"F0.wireOp",EDGE,"E207.MirrorCS");Q89=makeQuery(id+"F0.imprint","IMPRINT",FACE,{"disambiguationData":[TD([[makeQuery(id+"F0.imprint","IMPRINT",EDGE,{"derivedFrom":subQ0}),-1.0]])]});}
            var Q90;
            {var subQ0=sQuery(id+"F0.wireOp",EDGE,"E199.MirrorCS");Q90=makeQuery(id+"F0.imprint","IMPRINT",FACE,{"disambiguationData":[TD([[makeQuery(id+"F0.imprint","IMPRINT",EDGE,{"derivedFrom":subQ0}),1.0]])]});}
            extrude(context, id + "F1", {"entities" : qUnion([Q0, Q1, Q2, Q3, Q4, Q5, Q6, Q7, Q8, Q9, Q10, Q11, Q12, Q13, Q14, Q15, Q16, Q17, Q18, Q19, Q20, Q21, Q22, Q23, Q24, Q25, Q26, Q27, Q28, Q29, Q30, Q31, Q32, Q33, Q34, Q35, Q36, Q37, Q38, Q39, Q40, Q41, Q42, Q43, Q44, Q45, Q46, Q47, Q48, Q49, Q50, Q51, Q52, Q53, Q54, Q55, Q56, Q57, Q58, Q59, Q60, Q61, Q62, Q63, Q64, Q65, Q66, Q67, Q68, Q69, Q70, Q71, Q72, Q73, Q74, Q75, Q76, Q77, Q78, Q79, Q80, Q81, Q82, Q83, Q84, Q85, Q86, Q87, Q88, Q89, Q90]), "depth" : 1.52 * mm, "offsetDistance" : 25.4 * mm});
        }
    });
